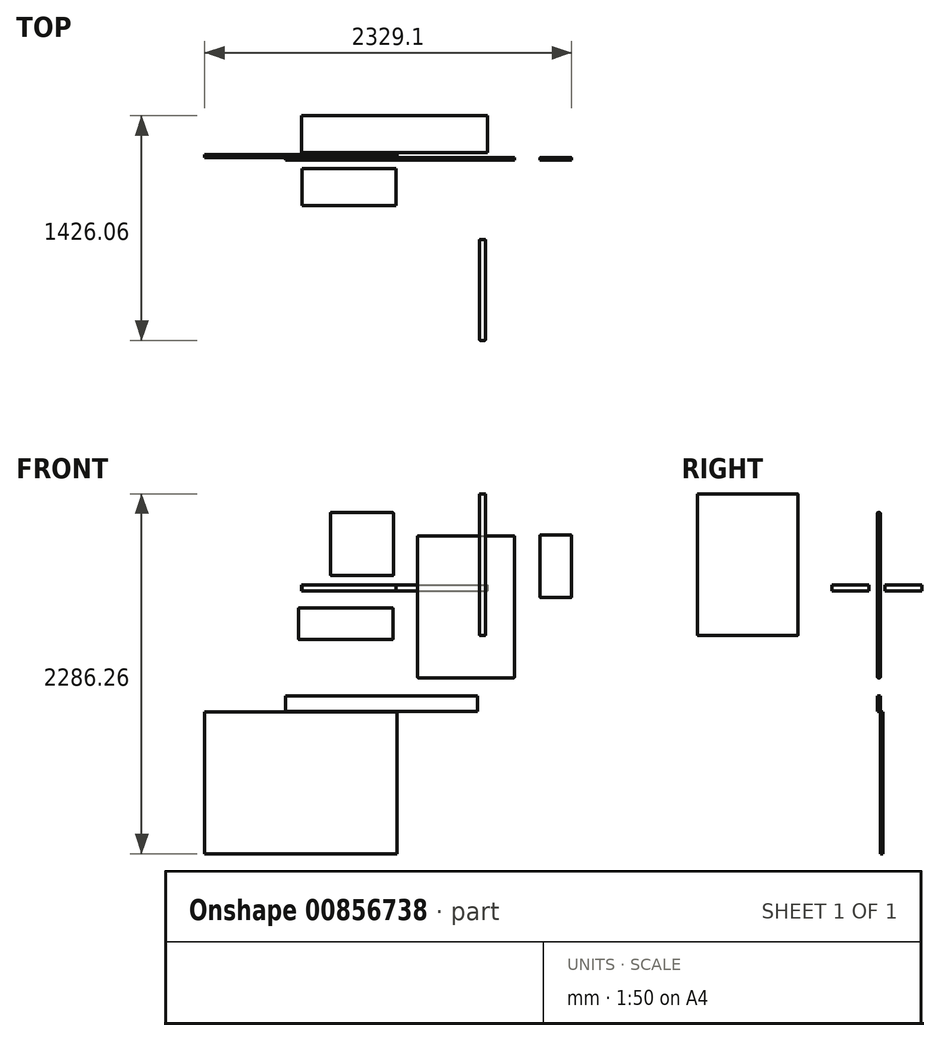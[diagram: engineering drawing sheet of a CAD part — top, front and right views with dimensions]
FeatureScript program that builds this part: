
annotation { "Feature Type Name" : "Feature", "Feature Type Description" : "" }
export const myFeature = defineFeature(function(context is Context, id is Id, definition is map)
    precondition{}
    {
        {
            var Q0;
            Q0=qCreatedBy(makeId("Front.planeOp"),FACE);
            var sketch = newSketch(context, id + "F0", { "sketchPlane" : qUnion([Q0])});
            skLineSegment(sketch, "E0.bottom", {"start": v(-394.44, 349.68) * mm, "end": v(220.56, 349.68) * mm});
            skLineSegment(sketch, "E0.top", {"start": v(-394.44, -550.32) * mm, "end": v(220.56, -550.32) * mm});
            skLineSegment(sketch, "E0.left", {"start": v(-394.44, 349.68) * mm, "end": v(-394.44, -550.32) * mm});
            skLineSegment(sketch, "E0.right", {"start": v(220.56, 349.68) * mm, "end": v(220.56, -550.32) * mm});
            skLineSegment(sketch, "E1.bottom", {"start": v(-947.07, 497.66) * mm, "end": v(-547.07, 497.66) * mm});
            skLineSegment(sketch, "E1.top", {"start": v(-947.07, 99.66) * mm, "end": v(-547.07, 99.66) * mm});
            skLineSegment(sketch, "E1.left", {"start": v(-947.07, 497.66) * mm, "end": v(-947.07, 99.66) * mm});
            skLineSegment(sketch, "E1.right", {"start": v(-547.07, 497.66) * mm, "end": v(-547.07, 99.66) * mm});
            skLineSegment(sketch, "E2.bottom", {"start": v(-1150.04, -108) * mm, "end": v(-550.04, -108) * mm});
            skLineSegment(sketch, "E2.top", {"start": v(-1150.04, -308) * mm, "end": v(-550.04, -308) * mm});
            skLineSegment(sketch, "E2.left", {"start": v(-1150.04, -108) * mm, "end": v(-1150.04, -308) * mm});
            skLineSegment(sketch, "E2.right", {"start": v(-550.04, -108) * mm, "end": v(-550.04, -308) * mm});
            skLineSegment(sketch, "E3.bottom", {"start": v(-1232.86, -665.92) * mm, "end": v(-12.86, -665.92) * mm});
            skLineSegment(sketch, "E3.top", {"start": v(-1232.86, -765.92) * mm, "end": v(-12.86, -765.92) * mm});
            skLineSegment(sketch, "E3.left", {"start": v(-1232.86, -665.92) * mm, "end": v(-1232.86, -765.92) * mm});
            skLineSegment(sketch, "E3.right", {"start": v(-12.86, -665.92) * mm, "end": v(-12.86, -765.92) * mm});
            skLineSegment(sketch, "E4.bottom", {"start": v(383.19, 356.45) * mm, "end": v(583.19, 356.45) * mm});
            skLineSegment(sketch, "E4.top", {"start": v(383.19, -41.55) * mm, "end": v(583.19, -41.55) * mm});
            skLineSegment(sketch, "E4.left", {"start": v(383.19, 356.45) * mm, "end": v(383.19, -41.55) * mm});
            skLineSegment(sketch, "E4.right", {"start": v(583.19, 356.45) * mm, "end": v(583.19, -41.55) * mm});
            skSolve(sketch);
        }
        {
            var Q0;
            Q0=makeQuery(id+"F0.imprint","IMPRINT",FACE,{"disambiguationData":[TD([[makeQuery(id+"F0.imprint","IMPRINT",EDGE,{"derivedFrom":sQuery(id+"F0.wireOp",EDGE,"E0.bottom")}),-1.0]])]});
            extrude(context, id + "F1", {"entities" : qUnion([Q0]), "depth" : 18 * mm, "offsetDistance" : 25 * mm});
        }
        {
            var Q0;
            Q0=makeQuery(id+"F1.opExtrude","CAP_EDGE",EDGE,{"disambiguationData":[OSD([sQuery(id+"F0.wireOp",EDGE,"E0.bottom")])],"isStart":false});
            var Q1;
            Q1=makeQuery(id+"F1.opExtrude","CAP_EDGE",EDGE,{"disambiguationData":[OSD([sQuery(id+"F0.wireOp",EDGE,"E0.left")])],"isStart":false});
            var Q2;
            Q2=makeQuery(id+"F1.opExtrude","CAP_EDGE",EDGE,{"disambiguationData":[OSD([sQuery(id+"F0.wireOp",EDGE,"E0.right")])],"isStart":false});
            var Q3;
            Q3=makeQuery(id+"F1.opExtrude","CAP_EDGE",EDGE,{"disambiguationData":[OSD([sQuery(id+"F0.wireOp",EDGE,"E0.top")])],"isStart":false});
            var Q4;
            Q4=makeQuery(id+"F1.opExtrude","SWEPT_EDGE",EDGE,{"disambiguationData":[OSD([sQuery(id+"F0.wireOp",EDGE,"E0.bottom"),sQuery(id+"F0.wireOp",EDGE,"E0.right")])]});
            var Q5;
            Q5=makeQuery(id+"F1.opExtrude","SWEPT_EDGE",EDGE,{"disambiguationData":[OSD([sQuery(id+"F0.wireOp",EDGE,"E0.bottom"),sQuery(id+"F0.wireOp",EDGE,"E0.left")])]});
            var Q6;
            Q6=makeQuery(id+"F1.opExtrude","SWEPT_EDGE",EDGE,{"disambiguationData":[OSD([sQuery(id+"F0.wireOp",EDGE,"E0.top"),sQuery(id+"F0.wireOp",EDGE,"E0.right")])]});
            var Q7;
            Q7=makeQuery(id+"F1.opExtrude","SWEPT_EDGE",EDGE,{"disambiguationData":[OSD([sQuery(id+"F0.wireOp",EDGE,"E0.top"),sQuery(id+"F0.wireOp",EDGE,"E0.left")])]});
            var Q8;
            Q8=makeQuery(id+"F1.opExtrude","CAP_EDGE",EDGE,{"disambiguationData":[OSD([sQuery(id+"F0.wireOp",EDGE,"E0.left")])],"isStart":true});
            var Q9;
            Q9=makeQuery(id+"F1.opExtrude","CAP_EDGE",EDGE,{"disambiguationData":[OSD([sQuery(id+"F0.wireOp",EDGE,"E0.top")])],"isStart":true});
            var Q10;
            Q10=makeQuery(id+"F1.opExtrude","CAP_EDGE",EDGE,{"disambiguationData":[OSD([sQuery(id+"F0.wireOp",EDGE,"E0.bottom")])],"isStart":true});
            var Q11;
            Q11=makeQuery(id+"F1.opExtrude","CAP_EDGE",EDGE,{"disambiguationData":[OSD([sQuery(id+"F0.wireOp",EDGE,"E0.right")])],"isStart":true});
            fillet(context, id + "F2", {"entities" : qUnion([Q0, Q1, Q2, Q3, Q4, Q5, Q6, Q7, Q8, Q9, Q10, Q11]), "radius" : 2.5 * mm, "tangentPropagation" : true, "allowEdgeOverflow" : false});
        }
        {
            var Q0;
            Q0=makeQuery(id+"F0.imprint","IMPRINT",FACE,{"disambiguationData":[TD([[makeQuery(id+"F0.imprint","IMPRINT",EDGE,{"derivedFrom":sQuery(id+"F0.wireOp",EDGE,"E1.bottom")}),-1.0]])]});
            var Q1;
            Q1=makeQuery(id+"F0.imprint","IMPRINT",FACE,{"disambiguationData":[TD([[makeQuery(id+"F0.imprint","IMPRINT",EDGE,{"derivedFrom":sQuery(id+"F0.wireOp",EDGE,"E2.bottom")}),-1.0]])]});
            extrude(context, id + "F3", {"entities" : qUnion([Q0, Q1]), "depth" : 18 * mm, "offsetDistance" : 25 * mm});
        }
        {
            var Q0;
            Q0=makeQuery(id+"F3.opExtrude","SWEPT_FACE",FACE,{"disambiguationData":[OSD([sQuery(id+"F0.wireOp",EDGE,"E1.bottom")])]});
            var Q1;
            Q1=makeQuery(id+"F3.opExtrude","CAP_FACE",FACE,{"disambiguationData":[OSD([sQuery(id+"F0.wireOp",EDGE,"E1.bottom"),sQuery(id+"F0.wireOp",EDGE,"E1.top"),sQuery(id+"F0.wireOp",EDGE,"E1.left"),sQuery(id+"F0.wireOp",EDGE,"E1.right")])],"isStart":false});
            var Q2;
            Q2=makeQuery(id+"F3.opExtrude","SWEPT_FACE",FACE,{"disambiguationData":[OSD([sQuery(id+"F0.wireOp",EDGE,"E1.top")])]});
            var Q3;
            Q3=makeQuery(id+"F3.opExtrude","SWEPT_FACE",FACE,{"disambiguationData":[OSD([sQuery(id+"F0.wireOp",EDGE,"E1.right")])]});
            var Q4;
            Q4=makeQuery(id+"F3.opExtrude","CAP_EDGE",EDGE,{"disambiguationData":[OSD([sQuery(id+"F0.wireOp",EDGE,"E1.bottom")])],"isStart":false});
            var Q5;
            Q5=makeQuery(id+"F3.opExtrude","CAP_EDGE",EDGE,{"disambiguationData":[OSD([sQuery(id+"F0.wireOp",EDGE,"E1.top")])],"isStart":false});
            var Q6;
            Q6=makeQuery(id+"F3.opExtrude","SWEPT_FACE",FACE,{"disambiguationData":[OSD([sQuery(id+"F0.wireOp",EDGE,"E2.bottom")])]});
            var Q7;
            Q7=makeQuery(id+"F3.opExtrude","CAP_FACE",FACE,{"disambiguationData":[OSD([sQuery(id+"F0.wireOp",EDGE,"E2.bottom"),sQuery(id+"F0.wireOp",EDGE,"E2.top"),sQuery(id+"F0.wireOp",EDGE,"E2.left"),sQuery(id+"F0.wireOp",EDGE,"E2.right")])],"isStart":false});
            var Q8;
            Q8=makeQuery(id+"F3.opExtrude","SWEPT_FACE",FACE,{"disambiguationData":[OSD([sQuery(id+"F0.wireOp",EDGE,"E2.top")])]});
            var Q9;
            Q9=makeQuery(id+"F3.opExtrude","SWEPT_FACE",FACE,{"disambiguationData":[OSD([sQuery(id+"F0.wireOp",EDGE,"E2.right")])]});
            var Q10;
            Q10=makeQuery(id+"F3.opExtrude","CAP_EDGE",EDGE,{"disambiguationData":[OSD([sQuery(id+"F0.wireOp",EDGE,"E2.bottom")])],"isStart":false});
            var Q11;
            Q11=makeQuery(id+"F3.opExtrude","CAP_EDGE",EDGE,{"disambiguationData":[OSD([sQuery(id+"F0.wireOp",EDGE,"E2.top")])],"isStart":false});
            var Q12;
            Q12=makeQuery(id+"F3.opExtrude","CAP_EDGE",EDGE,{"disambiguationData":[OSD([sQuery(id+"F0.wireOp",EDGE,"E1.right")])],"isStart":false});
            var Q13;
            Q13=makeQuery(id+"F3.opExtrude","CAP_FACE",FACE,{"disambiguationData":[OSD([sQuery(id+"F0.wireOp",EDGE,"E1.bottom"),sQuery(id+"F0.wireOp",EDGE,"E1.top"),sQuery(id+"F0.wireOp",EDGE,"E1.left"),sQuery(id+"F0.wireOp",EDGE,"E1.right")])],"isStart":true});
            var Q14;
            Q14=makeQuery(id+"F3.opExtrude","SWEPT_FACE",FACE,{"disambiguationData":[OSD([sQuery(id+"F0.wireOp",EDGE,"E1.left")])]});
            var Q15;
            Q15=makeQuery(id+"F3.opExtrude","CAP_EDGE",EDGE,{"disambiguationData":[OSD([sQuery(id+"F0.wireOp",EDGE,"E1.bottom")])],"isStart":true});
            var Q16;
            Q16=makeQuery(id+"F3.opExtrude","CAP_EDGE",EDGE,{"disambiguationData":[OSD([sQuery(id+"F0.wireOp",EDGE,"E1.top")])],"isStart":true});
            var Q17;
            Q17=makeQuery(id+"F3.opExtrude","CAP_FACE",FACE,{"disambiguationData":[OSD([sQuery(id+"F0.wireOp",EDGE,"E2.bottom"),sQuery(id+"F0.wireOp",EDGE,"E2.top"),sQuery(id+"F0.wireOp",EDGE,"E2.left"),sQuery(id+"F0.wireOp",EDGE,"E2.right")])],"isStart":true});
            var Q18;
            Q18=makeQuery(id+"F3.opExtrude","SWEPT_FACE",FACE,{"disambiguationData":[OSD([sQuery(id+"F0.wireOp",EDGE,"E2.left")])]});
            var Q19;
            Q19=makeQuery(id+"F3.opExtrude","CAP_EDGE",EDGE,{"disambiguationData":[OSD([sQuery(id+"F0.wireOp",EDGE,"E2.bottom")])],"isStart":true});
            var Q20;
            Q20=makeQuery(id+"F3.opExtrude","CAP_EDGE",EDGE,{"disambiguationData":[OSD([sQuery(id+"F0.wireOp",EDGE,"E2.top")])],"isStart":true});
            var Q21;
            Q21=makeQuery(id+"F3.opExtrude","CAP_EDGE",EDGE,{"disambiguationData":[OSD([sQuery(id+"F0.wireOp",EDGE,"E2.right")])],"isStart":false});
            var Q22;
            Q22=makeQuery(id+"F3.opExtrude","CAP_EDGE",EDGE,{"disambiguationData":[OSD([sQuery(id+"F0.wireOp",EDGE,"E1.left")])],"isStart":false});
            var Q23;
            Q23=makeQuery(id+"F3.opExtrude","CAP_EDGE",EDGE,{"disambiguationData":[OSD([sQuery(id+"F0.wireOp",EDGE,"E1.right")])],"isStart":true});
            var Q24;
            Q24=makeQuery(id+"F3.opExtrude","SWEPT_EDGE",EDGE,{"disambiguationData":[OSD([sQuery(id+"F0.wireOp",EDGE,"E1.bottom"),sQuery(id+"F0.wireOp",EDGE,"E1.left")])]});
            var Q25;
            Q25=makeQuery(id+"F3.opExtrude","SWEPT_EDGE",EDGE,{"disambiguationData":[OSD([sQuery(id+"F0.wireOp",EDGE,"E1.bottom"),sQuery(id+"F0.wireOp",EDGE,"E1.right")])]});
            var Q26;
            Q26=makeQuery(id+"F3.opExtrude","SWEPT_EDGE",EDGE,{"disambiguationData":[OSD([sQuery(id+"F0.wireOp",EDGE,"E1.top"),sQuery(id+"F0.wireOp",EDGE,"E1.left")])]});
            var Q27;
            Q27=makeQuery(id+"F3.opExtrude","SWEPT_EDGE",EDGE,{"disambiguationData":[OSD([sQuery(id+"F0.wireOp",EDGE,"E1.top"),sQuery(id+"F0.wireOp",EDGE,"E1.right")])]});
            var Q28;
            Q28=makeQuery(id+"F3.opExtrude","CAP_EDGE",EDGE,{"disambiguationData":[OSD([sQuery(id+"F0.wireOp",EDGE,"E1.left")])],"isStart":true});
            var Q29;
            Q29=makeQuery(id+"F3.opExtrude","SWEPT_EDGE",EDGE,{"disambiguationData":[OSD([sQuery(id+"F0.wireOp",EDGE,"E2.bottom"),sQuery(id+"F0.wireOp",EDGE,"E2.left")])]});
            var Q30;
            Q30=makeQuery(id+"F3.opExtrude","SWEPT_EDGE",EDGE,{"disambiguationData":[OSD([sQuery(id+"F0.wireOp",EDGE,"E2.bottom"),sQuery(id+"F0.wireOp",EDGE,"E2.right")])]});
            var Q31;
            Q31=makeQuery(id+"F3.opExtrude","SWEPT_EDGE",EDGE,{"disambiguationData":[OSD([sQuery(id+"F0.wireOp",EDGE,"E2.top"),sQuery(id+"F0.wireOp",EDGE,"E2.left")])]});
            var Q32;
            Q32=makeQuery(id+"F3.opExtrude","SWEPT_EDGE",EDGE,{"disambiguationData":[OSD([sQuery(id+"F0.wireOp",EDGE,"E2.top"),sQuery(id+"F0.wireOp",EDGE,"E2.right")])]});
            var Q33;
            Q33=makeQuery(id+"F3.opExtrude","CAP_EDGE",EDGE,{"disambiguationData":[OSD([sQuery(id+"F0.wireOp",EDGE,"E2.left")])],"isStart":true});
            var Q34;
            Q34=makeQuery(id+"F3.opExtrude","CAP_EDGE",EDGE,{"disambiguationData":[OSD([sQuery(id+"F0.wireOp",EDGE,"E2.left")])],"isStart":false});
            var Q35;
            Q35=makeQuery(id+"F3.opExtrude","CAP_EDGE",EDGE,{"disambiguationData":[OSD([sQuery(id+"F0.wireOp",EDGE,"E2.right")])],"isStart":true});
            fillet(context, id + "F4", {"entities" : qUnion([Q0, Q1, Q2, Q3, Q4, Q5, Q6, Q7, Q8, Q9, Q10, Q11, Q12, Q13, Q14, Q15, Q16, Q17, Q18, Q19, Q20, Q21, Q22, Q23, Q24, Q25, Q26, Q27, Q28, Q29, Q30, Q31, Q32, Q33, Q34, Q35]), "radius" : 2.5 * mm, "tangentPropagation" : true, "allowEdgeOverflow" : false});
        }
        {
            var Q0;
            Q0=qCreatedBy(makeId("Top.planeOp"),FACE);
            var sketch = newSketch(context, id + "F5", { "sketchPlane" : qUnion([Q0])});
            skLineSegment(sketch, "E5.bottom", {"start": v(-1129.86, 264.63) * mm, "end": v(50.14, 264.63) * mm});
            skLineSegment(sketch, "E5.top", {"start": v(-1129.86, 29.63) * mm, "end": v(50.14, 29.63) * mm});
            skLineSegment(sketch, "E5.left", {"start": v(-1129.86, 264.63) * mm, "end": v(-1129.86, 29.63) * mm});
            skLineSegment(sketch, "E5.right", {"start": v(50.14, 264.63) * mm, "end": v(50.14, 29.63) * mm});
            skLineSegment(sketch, "E6.bottom", {"start": v(-1126.86, -71.45) * mm, "end": v(-531.86, -71.45) * mm});
            skLineSegment(sketch, "E6.top", {"start": v(-1126.86, -306.45) * mm, "end": v(-531.86, -306.45) * mm});
            skLineSegment(sketch, "E6.left", {"start": v(-1126.86, -71.45) * mm, "end": v(-1126.86, -306.45) * mm});
            skLineSegment(sketch, "E6.right", {"start": v(-531.86, -71.45) * mm, "end": v(-531.86, -306.45) * mm});
            skSolve(sketch);
        }
        {
            var Q0;
            Q0 = qSketchRegion(id + "F5", true);
            extrude(context, id + "F6", {"entities" : qUnion([Q0]), "depth" : 38 * mm, "offsetDistance" : 25 * mm});
        }
        {
            var Q0;
            Q0=makeQuery(id+"F0.imprint","IMPRINT",FACE,{"disambiguationData":[TD([[makeQuery(id+"F0.imprint","IMPRINT",EDGE,{"derivedFrom":sQuery(id+"F0.wireOp",EDGE,"E3.bottom")}),-1.0]])]});
            extrude(context, id + "F7", {"entities" : qUnion([Q0]), "depth" : 18 * mm, "offsetDistance" : 25 * mm});
        }
        {
            var Q0;
            Q0=makeQuery(id+"F0.imprint","IMPRINT",FACE,{"disambiguationData":[TD([[makeQuery(id+"F0.imprint","IMPRINT",EDGE,{"derivedFrom":sQuery(id+"F0.wireOp",EDGE,"E4.bottom")}),-1.0]])]});
            extrude(context, id + "F8", {"entities" : qUnion([Q0]), "depth" : 18 * mm, "offsetDistance" : 25 * mm});
        }
        {
            var Q0;
            Q0=makeQuery(id+"F8.opExtrude","CAP_FACE",FACE,{"disambiguationData":[OSD([sQuery(id+"F0.wireOp",EDGE,"E4.bottom"),sQuery(id+"F0.wireOp",EDGE,"E4.top"),sQuery(id+"F0.wireOp",EDGE,"E4.left"),sQuery(id+"F0.wireOp",EDGE,"E4.right")])],"isStart":true});
            var Q1;
            Q1=makeQuery(id+"F8.opExtrude","CAP_FACE",FACE,{"disambiguationData":[OSD([sQuery(id+"F0.wireOp",EDGE,"E4.bottom"),sQuery(id+"F0.wireOp",EDGE,"E4.top"),sQuery(id+"F0.wireOp",EDGE,"E4.left"),sQuery(id+"F0.wireOp",EDGE,"E4.right")])],"isStart":false});
            var Q2;
            Q2=makeQuery(id+"F8.opExtrude","SWEPT_EDGE",EDGE,{"disambiguationData":[OSD([sQuery(id+"F0.wireOp",EDGE,"E4.bottom"),sQuery(id+"F0.wireOp",EDGE,"E4.right")])]});
            var Q3;
            Q3=makeQuery(id+"F8.opExtrude","SWEPT_EDGE",EDGE,{"disambiguationData":[OSD([sQuery(id+"F0.wireOp",EDGE,"E4.top"),sQuery(id+"F0.wireOp",EDGE,"E4.right")])]});
            var Q4;
            Q4=makeQuery(id+"F8.opExtrude","SWEPT_EDGE",EDGE,{"disambiguationData":[OSD([sQuery(id+"F0.wireOp",EDGE,"E4.top"),sQuery(id+"F0.wireOp",EDGE,"E4.left")])]});
            var Q5;
            Q5=makeQuery(id+"F8.opExtrude","SWEPT_EDGE",EDGE,{"disambiguationData":[OSD([sQuery(id+"F0.wireOp",EDGE,"E4.bottom"),sQuery(id+"F0.wireOp",EDGE,"E4.left")])]});
            fillet(context, id + "F9", {"entities" : qUnion([Q0, Q1, Q2, Q3, Q4, Q5]), "radius" : 3 * mm, "tangentPropagation" : true, "allowEdgeOverflow" : false});
        }
        {
            var Q0;
            Q0=makeQuery(id+"F1.opExtrude","CAP_FACE",FACE,{"disambiguationData":[OSD([sQuery(id+"F0.wireOp",EDGE,"E0.bottom"),sQuery(id+"F0.wireOp",EDGE,"E0.top"),sQuery(id+"F0.wireOp",EDGE,"E0.left"),sQuery(id+"F0.wireOp",EDGE,"E0.right")])],"isStart":true});
            var sketch = newSketch(context, id + "F10", { "sketchPlane" : qUnion([Q0])});
            skLineSegment(sketch, "E7.bottom", {"start": v(525.91, -768.45) * mm, "end": v(1745.91, -768.45) * mm});
            skLineSegment(sketch, "E7.top", {"start": v(525.91, -1668.45) * mm, "end": v(1745.91, -1668.45) * mm});
            skLineSegment(sketch, "E7.left", {"start": v(525.91, -768.45) * mm, "end": v(525.91, -1668.45) * mm});
            skLineSegment(sketch, "E7.right", {"start": v(1745.91, -768.45) * mm, "end": v(1745.91, -1668.45) * mm});
            skSolve(sketch);
        }
        {
            var Q0;
            Q0=makeQuery(id+"F10.imprint","IMPRINT",FACE,{"disambiguationData":[TD([[makeQuery(id+"F10.imprint","IMPRINT",EDGE,{"derivedFrom":sQuery(id+"F10.wireOp",EDGE,"E7.bottom")}),-1.0]])]});
            extrude(context, id + "F11", {"entities" : qUnion([Q0]), "depth" : 18 * mm, "offsetDistance" : 25 * mm});
        }
        {
            var Q0;
            Q0=qCreatedBy(makeId("Right.planeOp"),FACE);
            var sketch = newSketch(context, id + "F12", { "sketchPlane" : qUnion([Q0])});
            skLineSegment(sketch, "E8.bottom", {"start": v(-1161.43, 617.8) * mm, "end": v(-521.43, 617.8) * mm});
            skLineSegment(sketch, "E8.top", {"start": v(-1161.43, -282.2) * mm, "end": v(-521.43, -282.2) * mm});
            skLineSegment(sketch, "E8.left", {"start": v(-1161.43, 617.8) * mm, "end": v(-1161.43, -282.2) * mm});
            skLineSegment(sketch, "E8.right", {"start": v(-521.43, 617.8) * mm, "end": v(-521.43, -282.2) * mm});
            skSolve(sketch);
        }
        {
            var Q0;
            Q0=makeQuery(id+"F12.imprint","IMPRINT",FACE,{"disambiguationData":[TD([[makeQuery(id+"F12.imprint","IMPRINT",EDGE,{"derivedFrom":sQuery(id+"F12.wireOp",EDGE,"E8.bottom")}),-1.0]])]});
            extrude(context, id + "F13", {"entities" : qUnion([Q0]), "depth" : 38 * mm, "offsetDistance" : 25 * mm});
        }
        {
            var Q0;
            Q0=makeQuery(id+"F13.opExtrude","CAP_FACE",FACE,{"disambiguationData":[OSD([sQuery(id+"F12.wireOp",EDGE,"E8.bottom"),sQuery(id+"F12.wireOp",EDGE,"E8.top"),sQuery(id+"F12.wireOp",EDGE,"E8.left"),sQuery(id+"F12.wireOp",EDGE,"E8.right")])],"isStart":false});
            fillet(context, id + "F14", {"entities" : qUnion([Q0]), "radius" : 3 * mm, "tangentPropagation" : true, "allowEdgeOverflow" : false});
        }
        {
            var Q0;
            Q0=makeQuery(id+"F13.opExtrude","CAP_FACE",FACE,{"disambiguationData":[OSD([sQuery(id+"F12.wireOp",EDGE,"E8.bottom"),sQuery(id+"F12.wireOp",EDGE,"E8.top"),sQuery(id+"F12.wireOp",EDGE,"E8.left"),sQuery(id+"F12.wireOp",EDGE,"E8.right")])],"isStart":true});
            fillet(context, id + "F15", {"entities" : qUnion([Q0]), "radius" : 3 * mm, "tangentPropagation" : true, "allowEdgeOverflow" : false});
        }
        {
            var Q0;
            Q0=makeQuery(id+"F13.opExtrude","SWEPT_FACE",FACE,{"disambiguationData":[OSD([sQuery(id+"F12.wireOp",EDGE,"E8.left")])]});
            fillet(context, id + "F16", {"entities" : qUnion([Q0]), "radius" : 3 * mm, "tangentPropagation" : true, "allowEdgeOverflow" : false});
        }
        {
            var Q0;
            Q0=makeQuery(id+"F13.opExtrude","SWEPT_FACE",FACE,{"disambiguationData":[OSD([sQuery(id+"F12.wireOp",EDGE,"E8.right")])]});
            fillet(context, id + "F17", {"entities" : qUnion([Q0]), "radius" : 3 * mm, "tangentPropagation" : true, "allowEdgeOverflow" : false});
        }
    });
